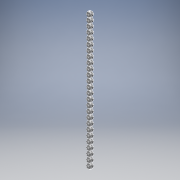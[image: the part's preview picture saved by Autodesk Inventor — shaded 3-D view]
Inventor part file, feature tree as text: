
AUTODESK INVENTOR PART (.ipt)
format: ipt  version: 2019 (Build 230136000, 136)  size: 182,272 bytes
history: native  units: mm
features: other x7, revolve x2, sketch x2, pattern_linear x1
ambient origin geometry x8: Origin, YZ Plane, XZ Plane, XY Plane, X Axis, Y Axis, Z Axis, Center Point
bodies: Solid1 (feature_tree)
feature tree (12):
  revolve  "Revolution1"  Angle=360.0deg
  revolve  "Revolution2"  [1 undecoded]
  pattern_linear  "Rectangular Pattern1"  [2 undecoded]
  other  "to_body_XY"
  other  "to_body_YZ"
  other  "to_body_ZX"
  other  "to_body_X"
  other  "to_body_Y"
  other  "to_body_Z"
  other  "to_body_Center"
  sketch  "Sketch_1"  dims[d0=360.0deg d1=360.0deg]
  sketch  "Sketch_2"  dims[d2=260.0mm d4=3.25mm d5=10.0mm d7=0.0mm]
note: 3 required parameter values undecoded (feature->parameter linkage not recoverable at this tier; creation-order binding heuristic only, values carry confidence <= 0.55)
